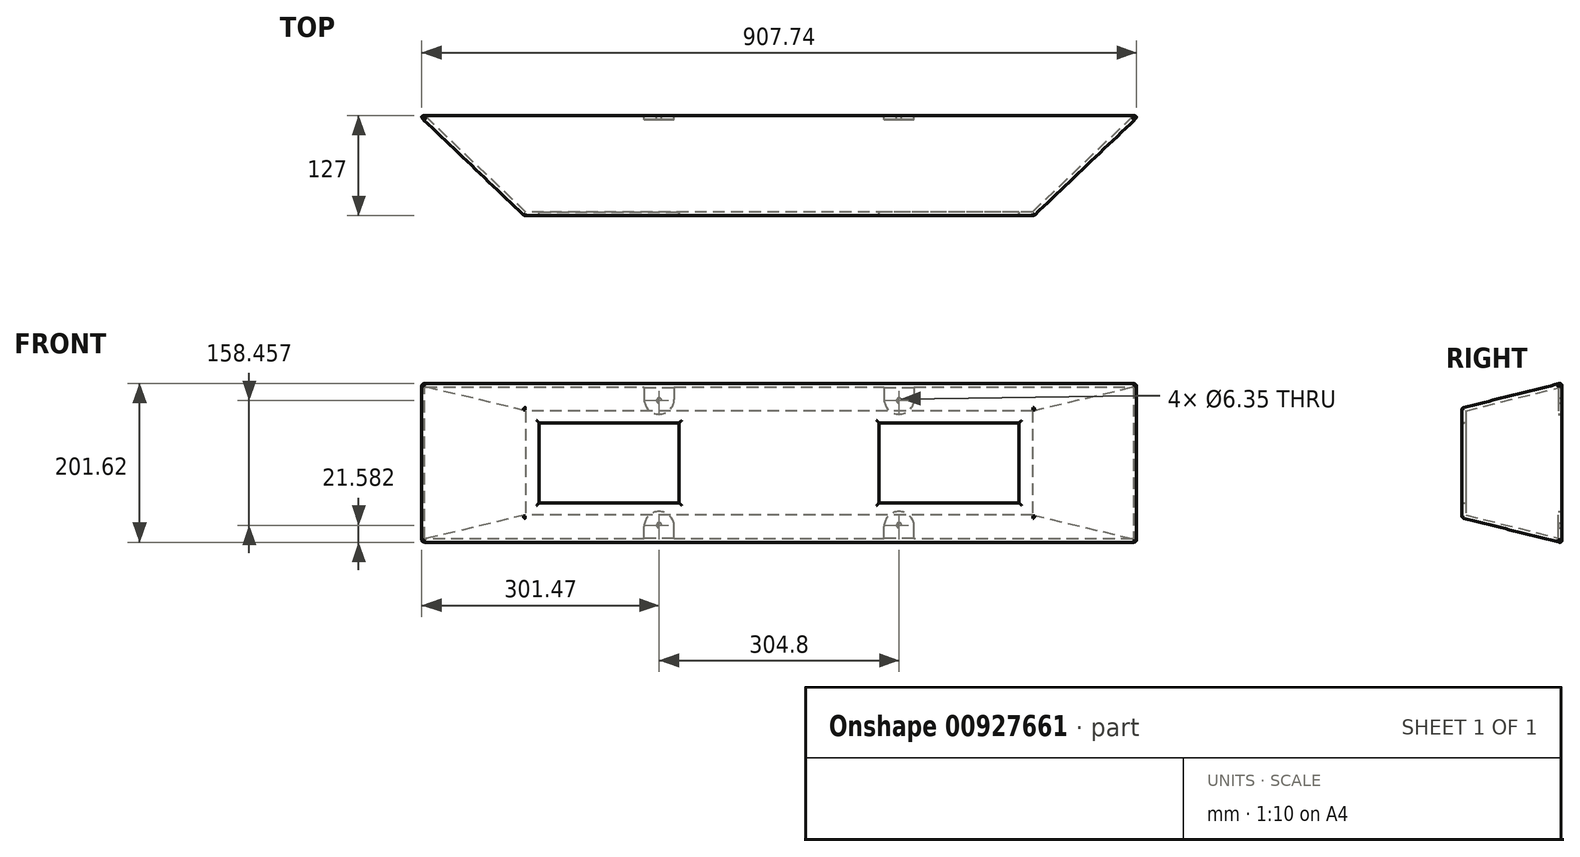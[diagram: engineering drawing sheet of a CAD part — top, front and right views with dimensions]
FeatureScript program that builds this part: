
annotation { "Feature Type Name" : "Feature", "Feature Type Description" : "" }
export const myFeature = defineFeature(function(context is Context, id is Id, definition is map)
    precondition{}
    {
        {
            var Q0;
            Q0=qCreatedBy(makeId("Front.planeOp"),FACE);
            var sketch = newSketch(context, id + "F0", { "sketchPlane" : qUnion([Q0])});
            skLineSegment(sketch, "E0.bottom", {"start": v(457.2, 101.6) * mm, "end": v(-457.2, 101.6) * mm});
            skLineSegment(sketch, "E0.top", {"start": v(457.2, -101.6) * mm, "end": v(-457.2, -101.6) * mm});
            skLineSegment(sketch, "E0.left", {"start": v(457.2, 101.6) * mm, "end": v(457.2, -101.6) * mm});
            skLineSegment(sketch, "E0.right", {"start": v(-457.2, 101.6) * mm, "end": v(-457.2, -101.6) * mm});
            skPoint(sketch, "E0.middle", {"position": v(0, 0) * mm});
            skSolve(sketch);
        }
        {
            var Q0;
            Q0 = qSketchRegion(id + "F0", true);
            extrude(context, id + "F1", {"entities" : qUnion([Q0]), "oppositeDirection" : true, "depth" : 127 * mm, "offsetDistance" : 25.4 * mm});
        }
        {
            var Q0;
            Q0=makeQuery(id+"F1.opExtrude","CAP_EDGE",EDGE,{"disambiguationData":[OSD([sQuery(id+"F0.wireOp",EDGE,"E0.right")])],"isStart":true});
            var Q1;
            Q1=makeQuery(id+"F1.opExtrude","CAP_EDGE",EDGE,{"disambiguationData":[OSD([sQuery(id+"F0.wireOp",EDGE,"E0.left")])],"isStart":true});
            chamfer(context, id + "F2", {"entities" : qUnion([Q0, Q1]), "chamferType" : ChamferType.TWO_OFFSETS, "width1" : 133.35 * mm, "oppositeDirection" : false, "width2" : 127 * mm, "tangentPropagation" : true});
        }
        {
            var Q0;
            Q0=makeQuery(id+"F1.opExtrude","CAP_EDGE",EDGE,{"disambiguationData":[OSD([sQuery(id+"F0.wireOp",EDGE,"E0.top")])],"isStart":true});
            var Q1;
            Q1=makeQuery(id+"F1.opExtrude","CAP_EDGE",EDGE,{"disambiguationData":[OSD([sQuery(id+"F0.wireOp",EDGE,"E0.bottom")])],"isStart":true});
            chamfer(context, id + "F3", {"entities" : qUnion([Q0, Q1]), "chamferType" : ChamferType.TWO_OFFSETS, "width1" : 127 * mm, "oppositeDirection" : false, "width2" : 31.75 * mm, "tangentPropagation" : true});
        }
        {
            var Q0;
            Q0=makeQuery(id+"F1.opExtrude","CAP_FACE",FACE,{"disambiguationData":[OSD([sQuery(id+"F0.wireOp",EDGE,"E0.bottom"),sQuery(id+"F0.wireOp",EDGE,"E0.top"),sQuery(id+"F0.wireOp",EDGE,"E0.left"),sQuery(id+"F0.wireOp",EDGE,"E0.right")])],"isStart":true});
            var Q1;
            Q1=makeQuery(id+"F1.opExtrude","CAP_FACE",FACE,{"disambiguationData":[OSD([sQuery(id+"F0.wireOp",EDGE,"E0.bottom"),sQuery(id+"F0.wireOp",EDGE,"E0.top"),sQuery(id+"F0.wireOp",EDGE,"E0.left"),sQuery(id+"F0.wireOp",EDGE,"E0.right")])],"isStart":false});
            shell(context, id + "F4", {"entities" : qUnion([Q0, Q1]), "thickness" : 4.76 * mm});
        }
        {
            var Q0;
            Q0=qCreatedBy(makeId("Front.planeOp"),FACE);
            var sketch = newSketch(context, id + "F5", { "sketchPlane" : qUnion([Q0])});
            skLineSegment(sketch, "E1.0", {"start": v(-304.8, 50.8) * mm, "end": v(-304.8, -50.8) * mm});
            skLineSegment(sketch, "E1.1", {"start": v(304.8, 50.8) * mm, "end": v(-304.8, 50.8) * mm});
            skLineSegment(sketch, "E1.2", {"start": v(304.8, -50.8) * mm, "end": v(304.8, 50.8) * mm});
            skLineSegment(sketch, "E1.3", {"start": v(-304.8, -50.8) * mm, "end": v(304.8, -50.8) * mm});
            skLineSegment(sketch, "E2.0", {"start": v(-323.85, 69.85) * mm, "end": v(-323.85, -69.85) * mm});
            skLineSegment(sketch, "E2.1", {"start": v(323.85, 69.85) * mm, "end": v(-323.85, 69.85) * mm});
            skLineSegment(sketch, "E2.2", {"start": v(323.85, -69.85) * mm, "end": v(323.85, 69.85) * mm});
            skLineSegment(sketch, "E2.3", {"start": v(-323.85, -69.85) * mm, "end": v(323.85, -69.85) * mm});
            skSolve(sketch);
        }
        {
            var Q0;
            Q0 = qSketchRegion(id + "F5", true);
            extrude(context, id + "F6", {"entities" : qUnion([Q0]), "operationType" : NewBodyOperationType.ADD, "oppositeDirection" : true, "depth" : 4.76 * mm, "offsetDistance" : 25.4 * mm});
        }
        {
            var Q0;
            Q0=qCreatedBy(makeId("Front.planeOp"),FACE);
            var sketch = newSketch(context, id + "F7", { "sketchPlane" : qUnion([Q0])});
            skLineSegment(sketch, "E3.bottom", {"start": v(127, 69.85) * mm, "end": v(-127, 69.85) * mm});
            skLineSegment(sketch, "E3.top", {"start": v(127, -69.85) * mm, "end": v(-127, -69.85) * mm});
            skLineSegment(sketch, "E3.left", {"start": v(127, 69.85) * mm, "end": v(127, -69.85) * mm});
            skLineSegment(sketch, "E3.right", {"start": v(-127, 69.85) * mm, "end": v(-127, -69.85) * mm});
            skPoint(sketch, "E3.middle", {"position": v(0, 0) * mm});
            skSolve(sketch);
        }
        {
            var Q0;
            Q0 = qSketchRegion(id + "F7", true);
            extrude(context, id + "F8", {"entities" : qUnion([Q0]), "operationType" : NewBodyOperationType.ADD, "oppositeDirection" : true, "depth" : 4.76 * mm, "offsetDistance" : 25.4 * mm});
        }
        {
            var Q0;
            Q0=makeQuery(id+"F1.opExtrude","CAP_FACE",FACE,{"disambiguationData":[OSD([sQuery(id+"F0.wireOp",EDGE,"E0.bottom"),sQuery(id+"F0.wireOp",EDGE,"E0.top"),sQuery(id+"F0.wireOp",EDGE,"E0.left"),sQuery(id+"F0.wireOp",EDGE,"E0.right")])],"isStart":false});
            var sketch = newSketch(context, id + "F9", { "sketchPlane" : qUnion([Q0])});
            skLineSegment(sketch, "E4.top", {"start": v(133.35, 61.77) * mm, "end": v(171.45, 61.77) * mm});
            skLineSegment(sketch, "E4.left", {"start": v(133.35, 96.7) * mm, "end": v(133.35, 61.77) * mm});
            skLineSegment(sketch, "E4.right", {"start": v(171.45, 96.7) * mm, "end": v(171.45, 61.77) * mm});
            skLineSegment(sketch, "E5.top", {"start": v(-171.45, 61.77) * mm, "end": v(-133.35, 61.77) * mm});
            skLineSegment(sketch, "E5.left", {"start": v(-171.45, 96.7) * mm, "end": v(-171.45, 61.77) * mm});
            skLineSegment(sketch, "E5.right", {"start": v(-133.35, 96.7) * mm, "end": v(-133.35, 61.77) * mm});
            skLineSegment(sketch, "E6.top", {"start": v(-171.45, -61.77) * mm, "end": v(-133.35, -61.77) * mm});
            skLineSegment(sketch, "E6.left", {"start": v(-171.45, -96.7) * mm, "end": v(-171.45, -61.77) * mm});
            skLineSegment(sketch, "E6.right", {"start": v(-133.35, -96.7) * mm, "end": v(-133.35, -61.77) * mm});
            skLineSegment(sketch, "E7.top", {"start": v(171.45, -61.77) * mm, "end": v(133.35, -61.77) * mm});
            skLineSegment(sketch, "E7.left", {"start": v(171.45, -96.7) * mm, "end": v(171.45, -61.77) * mm});
            skLineSegment(sketch, "E7.right", {"start": v(133.35, -96.7) * mm, "end": v(133.35, -61.77) * mm});
            skLineSegment(sketch, "E8", {"start": v(-171.45, 96.7) * mm, "end": v(-133.35, 96.7) * mm});
            skPoint(sketch, "E9.orphan", {"position": v(-171.45, 101.6) * mm});
            skLineSegment(sketch, "E10", {"start": v(133.35, 96.7) * mm, "end": v(171.45, 96.7) * mm});
            skPoint(sketch, "E4.bottom.start.orphan", {"position": v(133.35, 101.6) * mm});
            skLineSegment(sketch, "E11", {"start": v(133.35, -96.7) * mm, "end": v(171.45, -96.7) * mm});
            skPoint(sketch, "E7.bottom.start.orphan", {"position": v(171.45, -101.6) * mm});
            skLineSegment(sketch, "E12", {"start": v(-171.45, -96.7) * mm, "end": v(-133.35, -96.7) * mm});
            skPoint(sketch, "E6.bottom.start.orphan", {"position": v(-171.45, -101.6) * mm});
            skSolve(sketch);
        }
        {
            var Q0;
            Q0 = qSketchRegion(id + "F9", true);
            extrude(context, id + "F10", {"entities" : qUnion([Q0]), "operationType" : NewBodyOperationType.ADD, "oppositeDirection" : true, "depth" : 4.76 * mm, "offsetDistance" : 25.4 * mm});
        }
        {
            var Q0;
            Q0=makeQuery(id+"F10.boolean.opBoolean","MERGE",FACE,{"derivedFrom":[makeQuery(id+"F1.opExtrude","CAP_FACE",FACE,{"disambiguationData":[OSD([sQuery(id+"F0.wireOp",EDGE,"E0.bottom"),sQuery(id+"F0.wireOp",EDGE,"E0.top"),sQuery(id+"F0.wireOp",EDGE,"E0.left"),sQuery(id+"F0.wireOp",EDGE,"E0.right")])],"isStart":false}),makeQuery(id+"F10.opExtrude","CAP_FACE",FACE,{"disambiguationData":[OSD([sQuery(id+"F9.wireOp",EDGE,"E4.top"),sQuery(id+"F9.wireOp",EDGE,"E4.left"),sQuery(id+"F9.wireOp",EDGE,"E4.right"),sQuery(id+"F9.wireOp",EDGE,"E10")])],"isStart":true}),makeQuery(id+"F10.opExtrude","CAP_FACE",FACE,{"disambiguationData":[OSD([sQuery(id+"F9.wireOp",EDGE,"E5.top"),sQuery(id+"F9.wireOp",EDGE,"E5.left"),sQuery(id+"F9.wireOp",EDGE,"E5.right"),sQuery(id+"F9.wireOp",EDGE,"E8")])],"isStart":true}),makeQuery(id+"F10.opExtrude","CAP_FACE",FACE,{"disambiguationData":[OSD([sQuery(id+"F9.wireOp",EDGE,"E6.top"),sQuery(id+"F9.wireOp",EDGE,"E6.left"),sQuery(id+"F9.wireOp",EDGE,"E6.right"),sQuery(id+"F9.wireOp",EDGE,"E12")])],"isStart":true}),makeQuery(id+"F10.opExtrude","CAP_FACE",FACE,{"disambiguationData":[OSD([sQuery(id+"F9.wireOp",EDGE,"E7.top"),sQuery(id+"F9.wireOp",EDGE,"E7.left"),sQuery(id+"F9.wireOp",EDGE,"E7.right"),sQuery(id+"F9.wireOp",EDGE,"E11")])],"isStart":true})]});
            var sketch = newSketch(context, id + "F11", { "sketchPlane" : qUnion([Q0])});
            skCircle(sketch, "E13", {"center": v(152.4, 79.23) * mm, "radius": 3.18 * mm});
            skPoint(sketch, "E13.centerSnap0", {"position": v(133.35, 79.23) * mm});
            skPoint(sketch, "E13.centerSnap1", {"position": v(152.4, 61.77) * mm});
            skCircle(sketch, "E14", {"center": v(152.4, -79.23) * mm, "radius": 3.18 * mm});
            skPoint(sketch, "E14.centerSnap0", {"position": v(152.4, -61.77) * mm});
            skPoint(sketch, "E14.centerSnap1", {"position": v(133.35, -79.23) * mm});
            skCircle(sketch, "E15", {"center": v(-152.4, -79.23) * mm, "radius": 3.18 * mm});
            skPoint(sketch, "E15.centerSnap0", {"position": v(-171.45, -79.23) * mm});
            skPoint(sketch, "E15.centerSnap1", {"position": v(-152.4, -61.77) * mm});
            skCircle(sketch, "E16", {"center": v(-152.4, 79.23) * mm, "radius": 3.18 * mm});
            skPoint(sketch, "E16.centerSnap0", {"position": v(-152.4, 61.77) * mm});
            skPoint(sketch, "E16.centerSnap1", {"position": v(-171.45, 79.23) * mm});
            skSolve(sketch);
        }
        {
            var Q0;
            Q0 = qSketchRegion(id + "F11", true);
            extrude(context, id + "F12", {"entities" : qUnion([Q0]), "operationType" : NewBodyOperationType.REMOVE, "endBound" : BoundingType.UP_TO_NEXT, "oppositeDirection" : true, "depth" : 25.4 * mm, "offsetDistance" : 25.4 * mm});
        }
        {
            var Q0;
            Q0=makeQuery(id+"F10.opExtrude","SWEPT_EDGE",EDGE,{"disambiguationData":[OSD([sQuery(id+"F9.wireOp",EDGE,"E7.top"),sQuery(id+"F9.wireOp",EDGE,"E7.left")])]});
            var Q1;
            Q1=makeQuery(id+"F10.opExtrude","SWEPT_EDGE",EDGE,{"disambiguationData":[OSD([sQuery(id+"F9.wireOp",EDGE,"E7.top"),sQuery(id+"F9.wireOp",EDGE,"E7.right")])]});
            fillet(context, id + "F13", {"entities" : qUnion([Q0, Q1]), "radius" : 19.05 * mm, "tangentPropagation" : true, "allowEdgeOverflow" : false});
        }
        {
            var Q0;
            Q0=makeQuery(id+"F10.opExtrude","SWEPT_EDGE",EDGE,{"disambiguationData":[OSD([sQuery(id+"F9.wireOp",EDGE,"E4.top"),sQuery(id+"F9.wireOp",EDGE,"E4.right")])]});
            var Q1;
            Q1=makeQuery(id+"F10.opExtrude","SWEPT_EDGE",EDGE,{"disambiguationData":[OSD([sQuery(id+"F9.wireOp",EDGE,"E4.top"),sQuery(id+"F9.wireOp",EDGE,"E4.left")])]});
            fillet(context, id + "F14", {"entities" : qUnion([Q0, Q1]), "radius" : 19.05 * mm, "tangentPropagation" : true, "allowEdgeOverflow" : false});
        }
        {
            var Q0;
            Q0=makeQuery(id+"F10.opExtrude","SWEPT_EDGE",EDGE,{"disambiguationData":[OSD([sQuery(id+"F9.wireOp",EDGE,"E5.top"),sQuery(id+"F9.wireOp",EDGE,"E5.left")])]});
            var Q1;
            Q1=makeQuery(id+"F10.opExtrude","SWEPT_EDGE",EDGE,{"disambiguationData":[OSD([sQuery(id+"F9.wireOp",EDGE,"E5.top"),sQuery(id+"F9.wireOp",EDGE,"E5.right")])]});
            fillet(context, id + "F15", {"entities" : qUnion([Q0, Q1]), "radius" : 19.05 * mm, "tangentPropagation" : true, "allowEdgeOverflow" : false});
        }
        {
            var Q0;
            Q0=makeQuery(id+"F10.opExtrude","SWEPT_EDGE",EDGE,{"disambiguationData":[OSD([sQuery(id+"F9.wireOp",EDGE,"E6.top"),sQuery(id+"F9.wireOp",EDGE,"E6.left")])]});
            var Q1;
            Q1=makeQuery(id+"F10.opExtrude","SWEPT_EDGE",EDGE,{"disambiguationData":[OSD([sQuery(id+"F9.wireOp",EDGE,"E6.top"),sQuery(id+"F9.wireOp",EDGE,"E6.right")])]});
            fillet(context, id + "F16", {"entities" : qUnion([Q0, Q1]), "radius" : 19.05 * mm, "tangentPropagation" : true, "allowEdgeOverflow" : false});
        }
        {
            var Q0;
            Q0=makeQuery(id+"F3.opChamfer","BLEND_EDGE",EDGE,{"blendedFrom":[makeQuery(id+"F1.opExtrude","CAP_EDGE",EDGE,{"disambiguationData":[OSD([sQuery(id+"F0.wireOp",EDGE,"E0.bottom")])],"isStart":true}),makeQuery(id+"F2.opChamfer","BLEND_FACE",FACE,{"disambiguationData":[OSD([sQuery(id+"F0.wireOp",EDGE,"E0.left")])]})],"blendedInto":[makeQuery(id+"F2.opChamfer","BLEND_FACE",FACE,{"disambiguationData":[OSD([sQuery(id+"F0.wireOp",EDGE,"E0.left")])]})]});
            var Q1;
            Q1=makeQuery(id+"F2.opChamfer","BLEND_FACE",FACE,{"disambiguationData":[OSD([sQuery(id+"F0.wireOp",EDGE,"E0.left")])]});
            var Q2;
            {var subQ0=sQuery(id+"F0.wireOp",EDGE,"E0.bottom");Q2=makeQuery(id+"F3.opChamfer","BLEND_EDGE",EDGE,{"blendedFrom":[makeQuery(id+"F1.opExtrude","CAP_EDGE",EDGE,{"disambiguationData":[OSD([subQ0])],"isStart":true}),makeQuery(id+"F1.opExtrude","CAP_FACE",FACE,{"disambiguationData":[OSD([subQ0,sQuery(id+"F0.wireOp",EDGE,"E0.top"),sQuery(id+"F0.wireOp",EDGE,"E0.left"),sQuery(id+"F0.wireOp",EDGE,"E0.right")])],"isStart":true})],"blendedInto":[makeQuery(id+"F1.opExtrude","CAP_FACE",FACE,{"disambiguationData":[OSD([subQ0,sQuery(id+"F0.wireOp",EDGE,"E0.top"),sQuery(id+"F0.wireOp",EDGE,"E0.left"),sQuery(id+"F0.wireOp",EDGE,"E0.right")])],"isStart":true})]});}
            var Q3;
            {var subQ0=sQuery(id+"F0.wireOp",EDGE,"E0.top");Q3=makeQuery(id+"F3.opChamfer","BLEND_EDGE",EDGE,{"blendedFrom":[makeQuery(id+"F1.opExtrude","CAP_EDGE",EDGE,{"disambiguationData":[OSD([subQ0])],"isStart":true}),makeQuery(id+"F1.opExtrude","CAP_FACE",FACE,{"disambiguationData":[OSD([sQuery(id+"F0.wireOp",EDGE,"E0.bottom"),subQ0,sQuery(id+"F0.wireOp",EDGE,"E0.left"),sQuery(id+"F0.wireOp",EDGE,"E0.right")])],"isStart":true})],"blendedInto":[makeQuery(id+"F1.opExtrude","CAP_FACE",FACE,{"disambiguationData":[OSD([sQuery(id+"F0.wireOp",EDGE,"E0.bottom"),subQ0,sQuery(id+"F0.wireOp",EDGE,"E0.left"),sQuery(id+"F0.wireOp",EDGE,"E0.right")])],"isStart":true})]});}
            var Q4;
            {var subQ0=sQuery(id+"F0.wireOp",EDGE,"E0.right");Q4=makeQuery(id+"F2.opChamfer","BLEND_EDGE",EDGE,{"blendedFrom":[makeQuery(id+"F1.opExtrude","CAP_EDGE",EDGE,{"disambiguationData":[OSD([subQ0])],"isStart":true}),makeQuery(id+"F1.opExtrude","CAP_FACE",FACE,{"disambiguationData":[OSD([sQuery(id+"F0.wireOp",EDGE,"E0.bottom"),sQuery(id+"F0.wireOp",EDGE,"E0.top"),sQuery(id+"F0.wireOp",EDGE,"E0.left"),subQ0])],"isStart":true})],"blendedInto":[makeQuery(id+"F1.opExtrude","CAP_FACE",FACE,{"disambiguationData":[OSD([sQuery(id+"F0.wireOp",EDGE,"E0.bottom"),sQuery(id+"F0.wireOp",EDGE,"E0.top"),sQuery(id+"F0.wireOp",EDGE,"E0.left"),subQ0])],"isStart":true})]});}
            var Q5;
            Q5=makeQuery(id+"F3.opChamfer","BLEND_EDGE",EDGE,{"blendedFrom":[makeQuery(id+"F1.opExtrude","CAP_EDGE",EDGE,{"disambiguationData":[OSD([sQuery(id+"F0.wireOp",EDGE,"E0.top")])],"isStart":true}),makeQuery(id+"F2.opChamfer","BLEND_FACE",FACE,{"disambiguationData":[OSD([sQuery(id+"F0.wireOp",EDGE,"E0.right")])]})],"blendedInto":[makeQuery(id+"F2.opChamfer","BLEND_FACE",FACE,{"disambiguationData":[OSD([sQuery(id+"F0.wireOp",EDGE,"E0.right")])]})]});
            var Q6;
            Q6=makeQuery(id+"F3.opChamfer","BLEND_EDGE",EDGE,{"blendedFrom":[makeQuery(id+"F1.opExtrude","CAP_EDGE",EDGE,{"disambiguationData":[OSD([sQuery(id+"F0.wireOp",EDGE,"E0.bottom")])],"isStart":true}),makeQuery(id+"F2.opChamfer","BLEND_FACE",FACE,{"disambiguationData":[OSD([sQuery(id+"F0.wireOp",EDGE,"E0.right")])]})],"blendedInto":[makeQuery(id+"F2.opChamfer","BLEND_FACE",FACE,{"disambiguationData":[OSD([sQuery(id+"F0.wireOp",EDGE,"E0.right")])]})]});
            var Q7;
            {var subQ0=sQuery(id+"F0.wireOp",EDGE,"E0.right");Q7=makeQuery(id+"F2.opChamfer","BLEND_EDGE",EDGE,{"blendedFrom":[makeQuery(id+"F1.opExtrude","CAP_EDGE",EDGE,{"disambiguationData":[OSD([subQ0])],"isStart":true}),makeQuery(id+"F1.opExtrude","CAP_FACE",FACE,{"disambiguationData":[OSD([sQuery(id+"F0.wireOp",EDGE,"E0.bottom"),sQuery(id+"F0.wireOp",EDGE,"E0.top"),sQuery(id+"F0.wireOp",EDGE,"E0.left"),subQ0])],"isStart":false})],"blendedInto":[makeQuery(id+"F1.opExtrude","CAP_FACE",FACE,{"disambiguationData":[OSD([sQuery(id+"F0.wireOp",EDGE,"E0.bottom"),sQuery(id+"F0.wireOp",EDGE,"E0.top"),sQuery(id+"F0.wireOp",EDGE,"E0.left"),subQ0])],"isStart":false})]});}
            var Q8;
            {var subQ0=sQuery(id+"F0.wireOp",EDGE,"E0.top");Q8=makeQuery(id+"F3.opChamfer","BLEND_EDGE",EDGE,{"blendedFrom":[makeQuery(id+"F1.opExtrude","CAP_EDGE",EDGE,{"disambiguationData":[OSD([subQ0])],"isStart":true}),makeQuery(id+"F1.opExtrude","CAP_FACE",FACE,{"disambiguationData":[OSD([sQuery(id+"F0.wireOp",EDGE,"E0.bottom"),subQ0,sQuery(id+"F0.wireOp",EDGE,"E0.left"),sQuery(id+"F0.wireOp",EDGE,"E0.right")])],"isStart":false})],"blendedInto":[makeQuery(id+"F1.opExtrude","CAP_FACE",FACE,{"disambiguationData":[OSD([sQuery(id+"F0.wireOp",EDGE,"E0.bottom"),subQ0,sQuery(id+"F0.wireOp",EDGE,"E0.left"),sQuery(id+"F0.wireOp",EDGE,"E0.right")])],"isStart":false})]});}
            var Q9;
            {var subQ0=sQuery(id+"F0.wireOp",EDGE,"E0.bottom");Q9=makeQuery(id+"F3.opChamfer","BLEND_EDGE",EDGE,{"blendedFrom":[makeQuery(id+"F1.opExtrude","CAP_EDGE",EDGE,{"disambiguationData":[OSD([subQ0])],"isStart":true}),makeQuery(id+"F1.opExtrude","CAP_FACE",FACE,{"disambiguationData":[OSD([subQ0,sQuery(id+"F0.wireOp",EDGE,"E0.top"),sQuery(id+"F0.wireOp",EDGE,"E0.left"),sQuery(id+"F0.wireOp",EDGE,"E0.right")])],"isStart":false})],"blendedInto":[makeQuery(id+"F1.opExtrude","CAP_FACE",FACE,{"disambiguationData":[OSD([subQ0,sQuery(id+"F0.wireOp",EDGE,"E0.top"),sQuery(id+"F0.wireOp",EDGE,"E0.left"),sQuery(id+"F0.wireOp",EDGE,"E0.right")])],"isStart":false})]});}
            fillet(context, id + "F17", {"entities" : qUnion([Q0, Q1, Q2, Q3, Q4, Q5, Q6, Q7, Q8, Q9]), "radius" : 3.17 * mm, "tangentPropagation" : true, "rho" : 0.5, "crossSection" : FilletCrossSection.CONIC, "allowEdgeOverflow" : false});
        }
        {
            var Q0;
            Q0=makeQuery(id+"F6.opExtrude","CAP_EDGE",EDGE,{"disambiguationData":[OSD([sQuery(id+"F5.wireOp",EDGE,"E1.0")])],"isStart":true});
            var Q1;
            {var subQ0=sQuery(id+"F5.wireOp",EDGE,"E1.1");var subQ1=sQuery(id+"F5.wireOp",EDGE,"E1.0");Q1=makeQuery(id+"F8.boolean.opBoolean","SPLIT",EDGE,{"disambiguationData":[TD([makeQuery(id+"F6.opExtrude","SWEPT_FACE",FACE,{"disambiguationData":[OSD([subQ1])]})])],"derivedFrom":makeQuery(id+"F6.opExtrude","CAP_EDGE",EDGE,{"disambiguationData":[OSD([subQ0])],"isStart":true})});}
            var Q2;
            {var subQ0=sQuery(id+"F5.wireOp",EDGE,"E1.3");var subQ1=sQuery(id+"F5.wireOp",EDGE,"E1.0");Q2=makeQuery(id+"F8.boolean.opBoolean","SPLIT",EDGE,{"disambiguationData":[TD([makeQuery(id+"F6.opExtrude","SWEPT_FACE",FACE,{"disambiguationData":[OSD([subQ1])]})])],"derivedFrom":makeQuery(id+"F6.opExtrude","CAP_EDGE",EDGE,{"disambiguationData":[OSD([subQ0])],"isStart":true})});}
            var Q3;
            Q3=makeQuery(id+"F8.opExtrude","CAP_EDGE",EDGE,{"disambiguationData":[OSD([sQuery(id+"F7.wireOp",EDGE,"E3.right")])],"isStart":true});
            fillet(context, id + "F18", {"entities" : qUnion([Q0, Q1, Q2, Q3]), "radius" : 3.17 * mm, "tangentPropagation" : true, "allowEdgeOverflow" : false});
        }
        {
            var Q0;
            Q0=makeQuery(id+"F8.opExtrude","CAP_EDGE",EDGE,{"disambiguationData":[OSD([sQuery(id+"F7.wireOp",EDGE,"E3.left")])],"isStart":true});
            var Q1;
            {var subQ0=sQuery(id+"F5.wireOp",EDGE,"E1.2");var subQ1=sQuery(id+"F5.wireOp",EDGE,"E1.3");Q1=makeQuery(id+"F8.boolean.opBoolean","SPLIT",EDGE,{"disambiguationData":[TD([makeQuery(id+"F6.opExtrude","SWEPT_FACE",FACE,{"disambiguationData":[OSD([subQ0])]})])],"derivedFrom":makeQuery(id+"F6.opExtrude","CAP_EDGE",EDGE,{"disambiguationData":[OSD([subQ1])],"isStart":true})});}
            var Q2;
            Q2=makeQuery(id+"F6.opExtrude","CAP_EDGE",EDGE,{"disambiguationData":[OSD([sQuery(id+"F5.wireOp",EDGE,"E1.2")])],"isStart":true});
            var Q3;
            {var subQ0=sQuery(id+"F5.wireOp",EDGE,"E1.2");var subQ1=sQuery(id+"F5.wireOp",EDGE,"E1.1");Q3=makeQuery(id+"F8.boolean.opBoolean","SPLIT",EDGE,{"disambiguationData":[TD([makeQuery(id+"F6.opExtrude","SWEPT_FACE",FACE,{"disambiguationData":[OSD([subQ0])]})])],"derivedFrom":makeQuery(id+"F6.opExtrude","CAP_EDGE",EDGE,{"disambiguationData":[OSD([subQ1])],"isStart":true})});}
            fillet(context, id + "F19", {"entities" : qUnion([Q0, Q1, Q2, Q3]), "radius" : 3.17 * mm, "tangentPropagation" : true, "allowEdgeOverflow" : false});
        }
    });
